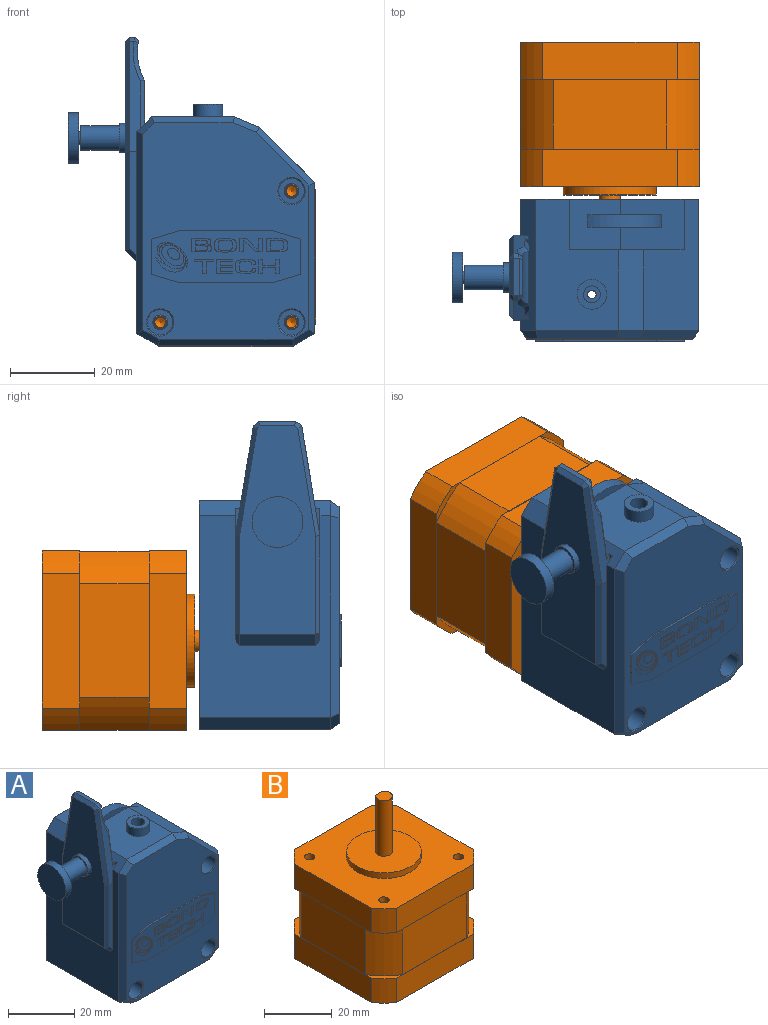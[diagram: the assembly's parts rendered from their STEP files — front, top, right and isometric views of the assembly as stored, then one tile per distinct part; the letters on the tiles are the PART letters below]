
ASSEMBLY  parts=2 mates=1
PART A: 276 faces, bbox 58.2x33.6x72.9 mm
  f0: cone r=3mm half-angle=45deg, axis (0,-1,0), area 6.9mm2, adj f4,f23
  f1: cone r=3mm half-angle=45deg, axis (0,-1,0), area 6.9mm2, adj f3,f23
  f2: cone r=3mm half-angle=45deg, axis (0,-1,0), area 6.9mm2, adj f5,f23
  f3: cylinder r=3mm len=6mm, axis (0,-1,0), area 80.1mm2, adj f1,f92
  f4: cylinder r=3mm len=6mm, axis (0,-1,0), area 80.1mm2, adj f0,f91
  f5: cylinder r=3mm len=6mm, axis (0,-1,0), area 80.1mm2, adj f2,f90
  f6: cylinder r=11mm len=22mm, axis (0,1,0), area 138.2mm2, adj f29,f89
  f7: cylinder r=1.75mm len=10.5mm, axis (1,0,0), area 115.5mm2, adj f85,f88
  f8: cylinder r=1.5mm len=11mm, axis (1,0,0), area 103.7mm2, adj f87,f88
  f9: cylinder r=6mm len=12mm, axis (1,0,0), area 94.2mm2, adj f86,f87
  f10: cylinder r=2.88mm len=9mm, axis (1,0,0), area 162.6mm2, adj f84,f85
  f11: cylinder r=3.5mm len=7mm, axis (1,0,0), area 33mm2, adj f56,f84
  f12: cylinder r=2mm len=4mm, axis (0,0,-1), area 37.7mm2, adj f22,f52
  f13: cylinder r=3.5mm len=7mm, axis (0,0,-1), area 66mm2, adj f27,f52
  f14: cylinder r=1mm len=51mm, axis (0,0,-1), area 320.4mm2, adj f22,f51
  f15: cylinder r=8mm len=16mm, axis (0,0,-1), area 150.8mm2, adj f25,f51
  f16: cylinder r=1.75mm len=28.5mm, axis (0,1,0), area 313.4mm2, adj f29,f90
  f17: cylinder r=1.75mm len=28.5mm, axis (0,1,0), area 313.4mm2, adj f29,f91
  f18: cylinder r=1.75mm len=28.5mm, axis (0,1,0), area 313.4mm2, adj f29,f92
  f19: plane 35.32x12.32mm, normal (0,-1,0), area 302.9mm2, adj f43,f44,f45,f46,f47,f48,f49,f50
  f20: plane 15x12mm, normal (0,0,1), area 150.6mm2, adj f21,f28,f29,f93,f94,f95,f96
  f21: plane 12x12mm, normal (0.71,0,0.71), area 171.1mm2, adj f20,f27,f29,f93,f94,f95,f96
  f22: plane 4x4mm, normal (0,0,1), area 9.4mm2, adj f12,f14
  f23: plane 51.2x39.2mm, normal (0,-1,0), area 1375.8mm2, adj f0,f1,f2,f34,f35,f36,f37,f38
  f24: plane 35.61x31mm, normal (1,0,0), area 1104mm2, adj f28,f29,f33,f40
  f25: plane 32x31mm, normal (0,0,-1), area 790.9mm2, adj f15,f29,f32,f33,f41
  f26: plane 47.61x31mm, normal (-1,0,0), area 863.4mm2, adj f29,f30,f32,f37,f53,f54,f55,f61
  f27: plane 31x19.5mm, normal (0,0,1), area 428mm2, adj f13,f21,f29,f30,f31,f34,f93
  f28: plane 31x13.03mm, normal (0.71,0,0.71), area 409.4mm2, adj f20,f24,f29,f31,f38,f93
  f29: plane 54x42mm, normal (0,1,0), area 1538.3mm2, adj f6,f16,f17,f18,f20,f21,f24,f25
  f30: plane 31x3.5mm, normal (-0.71,0,0.71), area 104mm2, adj f26,f27,f29,f35,f59,f60,f61,f62
  f31: plane 19x5.98mm, normal (0.38,0,0.92), area 122.9mm2, adj f27,f28,f36,f93
  f32: plane 31x5mm, normal (-0.5,0,-0.87), area 179mm2, adj f25,f26,f29,f39
  f33: plane 31x5mm, normal (0.5,0,-0.87), area 179mm2, adj f24,f25,f29,f42
  f34: plane 19.5x2mm, normal (0,-0.57,0.82), area 46.6mm2, adj f23,f27,f35,f36
  f35: plane 4.08x4.08mm, normal (-0.58,-0.57,0.58), area 10.7mm2, adj f23,f30,f34,f37
  f36: plane 6.25x3.66mm, normal (0.31,-0.57,0.76), area 15.1mm2, adj f23,f31,f34,f38
  f37: plane 47.61x2mm, normal (-0.82,-0.57,0), area 114.6mm2, adj f23,f26,f35,f39
  f38: plane 13.82x13.61mm, normal (0.58,-0.57,0.58), area 43.9mm2, adj f23,f28,f36,f40
  f39: plane 5.38x3.7mm, normal (-0.41,-0.57,-0.71), area 12.7mm2, adj f23,f32,f37,f41
  f40: plane 35.61x2mm, normal (0.82,-0.57,0), area 85.3mm2, adj f23,f24,f38,f42
  f41: plane 32x2mm, normal (0,-0.57,-0.82), area 77.2mm2, adj f23,f25,f39,f42
  f42: plane 5.38x3.7mm, normal (0.41,-0.57,-0.71), area 12.7mm2, adj f23,f33,f40,f41
  f43: plane 6.66x2mm, normal (0.29,0,-0.96), area 3.5mm2, adj f19,f23,f44,f50
  f44: plane 21.99x0.5mm, normal (0,0,-1), area 11mm2, adj f19,f23,f43,f45
  f45: plane 6.66x2mm, normal (-0.29,0,-0.96), area 3.5mm2, adj f19,f23,f44,f46
  f46: plane 8.3x0.5mm, normal (-1,0,0), area 4.2mm2, adj f19,f23,f45,f47
  f47: plane 6.66x2mm, normal (-0.29,0,0.96), area 3.5mm2, adj f19,f23,f46,f48
  f48: plane 21.99x0.5mm, normal (0,0,1), area 11mm2, adj f19,f23,f47,f49
  f49: plane 6.66x2mm, normal (0.29,0,0.96), area 3.5mm2, adj f19,f23,f48,f50
  f50: plane 8.3x0.5mm, normal (1,0,0), area 4.2mm2, adj f19,f23,f43,f49
  f51: plane 16x16mm, normal (0,0,-1), area 197.9mm2, adj f14,f15
  f52: plane 7x7mm, normal (0,0,1), area 25.9mm2, adj f12,f13
  f53: plane 24.54x1.7mm, normal (0,-1,0), area 40.3mm2, adj f26,f65,f82,f83
  f54: plane 24.54x1.7mm, normal (0,1,0), area 40.3mm2, adj f26,f62,f75,f76
  f55: plane 18x2.7mm, normal (-0.71,0,-0.71), area 68.7mm2, adj f26,f56,f75,f83
  f56: plane 49.25x18mm, normal (-1,0,0), area 734.7mm2, adj f11,f55,f76,f77,f78,f79,f80,f81
  f57: plane 8.82x1.26mm, normal (0,0,1), area 11.1mm2, adj f66,f67,f70,f71,f72,f79
  f58: cylinder r=13.85mm len=12.41mm, axis (0,1,0), area 103.2mm2, adj f59,f68,f69,f70,f71,f72,f73,f74
  f59: plane 15.8x10.33mm, normal (1,0,0), area 145.5mm2, adj f30,f58,f68,f74
  f60: plane 6.55x1.09mm, normal (-1,0,0), area 3.6mm2, adj f30,f61,f62
  f61: plane 6.55x1.8mm, normal (0,-1,0), area 10.2mm2, adj f26,f30,f60,f62
  f62: plane 25.8x4.28mm, normal (0,0.99,0.16), area 59.8mm2, adj f30,f54,f60,f61,f66,f73,f74,f77
  f63: plane 6.55x1.09mm, normal (-1,0,0), area 3.6mm2, adj f30,f64,f65
  f64: plane 6.55x1.8mm, normal (0,1,0), area 10.2mm2, adj f26,f30,f63,f65
  f65: plane 26.01x4.32mm, normal (0,-0.99,0.16), area 60mm2, adj f30,f53,f63,f64,f67,f68,f69,f81
  f66: plane 1.23x1.2mm, normal (0,0.71,0.71), area 1.9mm2, adj f57,f62,f72,f73,f78
  f67: plane 1.38x1.24mm, normal (0,-0.58,0.81), area 1.9mm2, adj f57,f65,f69,f70,f80
  f68: plane 11.38x2.9mm, normal (0.71,-0.7,0.12), area 15.5mm2, adj f30,f58,f59,f65,f69
  f69: bspline ~9.52x2.69mm, area 13.8mm2, adj f58,f65,f67,f68,f70
  f70: bspline ~1.95x1.79mm, area 1.4mm2, adj f57,f58,f67,f69,f71
  f71: plane 8.79x0.84mm, normal (0.71,0,0.71), area 9.7mm2, adj f57,f58,f70,f72
  f72: bspline ~1.96x1.86mm, area 1.4mm2, adj f57,f58,f66,f71,f73
  f73: bspline ~9.42x2.69mm, area 13.7mm2, adj f58,f62,f66,f72,f74
  f74: plane 11.39x2.91mm, normal (0.71,0.7,0.12), area 15.5mm2, adj f30,f58,f59,f62,f73
  f75: plane 3.11x2.7mm, normal (-0.5,0.71,-0.5), area 4.4mm2, adj f26,f54,f55,f76
  f76: plane 23.25x1mm, normal (-0.71,0.71,0), area 32.5mm2, adj f54,f56,f75,f77
  f77: plane 25.88x5.22mm, normal (-0.71,0.7,0.12), area 36.7mm2, adj f56,f62,f76,f78
  f78: plane 1.68x1.61mm, normal (-0.71,0.5,0.5), area 1.9mm2, adj f56,f66,f77,f79
  f79: plane 8.82x1mm, normal (-0.71,0,0.71), area 12mm2, adj f56,f57,f78,f80
  f80: plane 1.7x1.56mm, normal (-0.71,-0.41,0.58), area 1.9mm2, adj f56,f67,f79,f81
  f81: plane 26.09x5.24mm, normal (-0.71,-0.7,0.12), area 36.9mm2, adj f56,f65,f80,f82
  f82: plane 23.25x1mm, normal (-0.71,-0.71,0), area 32.5mm2, adj f53,f56,f81,f83
  f83: plane 3.11x2.7mm, normal (-0.5,-0.71,-0.5), area 4.4mm2, adj f26,f53,f55,f82
  f84: plane 7x7mm, normal (-1,0,0), area 12.5mm2, adj f10,f11
  f85: plane 5.75x5.75mm, normal (-1,0,0), area 16.3mm2, adj f7,f10
  f86: plane 12x12mm, normal (-1,0,0), area 113.1mm2, adj f9
  f87: plane 12x12mm, normal (1,0,0), area 106mm2, adj f8,f9
  f88: plane 3.5x3.5mm, normal (-1,0,0), area 2.6mm2, adj f7,f8
  f89: plane 22x22mm, normal (0,1,0), area 380.1mm2, adj f6
  f90: plane 6x6mm, normal (0,-1,0), area 18.7mm2, adj f5,f16
  f91: plane 6x6mm, normal (0,-1,0), area 18.7mm2, adj f4,f17
  f92: plane 6x6mm, normal (0,-1,0), area 18.7mm2, adj f3,f18
  f93: plane 27x12mm, normal (0,1,0), area 175.7mm2, adj f20,f21,f27,f28,f31
  f94: cylinder r=13mm len=17.46mm, axis (0,1,0), area 64.2mm2, adj f20,f21,f95,f96
  f95: plane 17.46x8.75mm, normal (0,-1,0), area 92.5mm2, adj f20,f21,f94
  f96: plane 17.46x8.75mm, normal (0,1,0), area 92.5mm2, adj f20,f21,f94
  f97: extruded ~1.55x0.73mm, area 0.2mm2, adj f19,f98,f105,f106
  f98: extruded ~1.11x0.12mm, area 0.1mm2, adj f19,f97,f99,f106
  f99: extruded ~0.75x0.1mm, area 0.1mm2, adj f19,f98,f100,f106
  f100: extruded ~1.46x0.61mm, area 0.2mm2, adj f19,f99,f101,f106
  f101: extruded ~2.8x1.93mm, area 0.4mm2, adj f19,f100,f102,f106
  f102: extruded ~2.12x0.3mm, area 0.2mm2, adj f19,f101,f103,f106
  f103: extruded ~0.61x0.21mm, area 0.1mm2, adj f19,f102,f104,f106
  f104: extruded ~2.24x0.4mm, area 0.2mm2, adj f19,f103,f105,f106
  f105: extruded ~1.92x1.61mm, area 0.3mm2, adj f19,f97,f104,f106
  f106: plane 5.64x4.71mm, normal (0,-1,0), area 1.5mm2, adj f97,f98,f99,f100,f101,f102,f103,f104
  f107: plane 0.9x0.1mm, normal (0,0,-1), area 0.1mm2, adj f19,f108,f114,f115
  f108: plane 2.72x0.1mm, normal (1,0,0), area 0.3mm2, adj f19,f107,f109,f115
  f109: plane 1.82x0.1mm, normal (0,0,-1), area 0.2mm2, adj f19,f108,f110,f115
  f110: plane 0.44x0.1mm, normal (1,0,0), area 0mm2, adj f19,f109,f111,f115
  f111: plane 4.51x0.1mm, normal (0,0,1), area 0.5mm2, adj f19,f110,f112,f115
  f112: plane 0.44x0.1mm, normal (-1,0,0), area 0mm2, adj f19,f111,f113,f115
  f113: plane 1.79x0.1mm, normal (0,0,-1), area 0.2mm2, adj f19,f112,f114,f115
  f114: plane 2.72x0.1mm, normal (-1,0,0), area 0.3mm2, adj f19,f107,f113,f115
  f115: plane 4.51x3.15mm, normal (0,-1,0), area 4.4mm2, adj f107,f108,f109,f110,f111,f112,f113,f114
  f116: plane 2.85x0.1mm, normal (0,0,1), area 0.3mm2, adj f19,f117,f127,f128
  f117: plane 0.94x0.1mm, normal (1,0,0), area 0.1mm2, adj f19,f116,f118,f128
  f118: plane 2.99x0.1mm, normal (0,0,-1), area 0.3mm2, adj f19,f117,f119,f128
  f119: plane 0.41x0.1mm, normal (1,0,0), area 0mm2, adj f19,f118,f120,f128
  f120: plane 3.88x0.1mm, normal (0,0,1), area 0.4mm2, adj f19,f119,f121,f128
  f121: plane 3.15x0.1mm, normal (-1,0,0), area 0.3mm2, adj f19,f120,f122,f128
  f122: plane 3.9x0.1mm, normal (0,0,-1), area 0.4mm2, adj f19,f121,f123,f128
  f123: plane 0.41x0.1mm, normal (1,0,0), area 0mm2, adj f19,f122,f124,f128
  f124: plane 3x0.1mm, normal (0,0,1), area 0.3mm2, adj f19,f123,f125,f128
  f125: plane 1.03x0.1mm, normal (1,0,0), area 0.1mm2, adj f19,f124,f126,f128
  f126: plane 2.85x0.1mm, normal (0,0,-1), area 0.3mm2, adj f19,f125,f127,f128
  f127: plane 0.37x0.1mm, normal (1,0,0), area 0mm2, adj f19,f116,f126,f128
  f128: plane 3.9x3.15mm, normal (0,-1,0), area 6.3mm2, adj f116,f117,f118,f119,f120,f121,f122,f123
  f129: extruded ~2.07x0.23mm, area 0.2mm2, adj f19,f130,f150,f151
  f130: extruded ~0.78x0.36mm, area 0.1mm2, adj f19,f129,f131,f151
  f131: plane 0.11x0.1mm, normal (1,0,0), area 0mm2, adj f19,f130,f132,f151
  f132: plane 0.9x0.1mm, normal (0,0,1), area 0.1mm2, adj f19,f131,f133,f151
  f133: cylinder r=0.76mm len=0.15mm, axis (0,1,0), area 0mm2, adj f19,f132,f134,f151
  f134: extruded ~1.53x0.55mm, area 0.2mm2, adj f19,f133,f135,f151
  f135: extruded ~1.33x0.25mm, area 0.1mm2, adj f19,f134,f136,f151
  f136: extruded ~1.24x0.16mm, area 0.1mm2, adj f19,f135,f137,f151
  f137: extruded ~0.77x0.26mm, area 0.1mm2, adj f19,f136,f138,f151
  f138: extruded ~1.48x0.13mm, area 0.1mm2, adj f19,f137,f139,f151
  f139: extruded ~1.06x0.16mm, area 0.1mm2, adj f19,f138,f140,f151
  f140: extruded ~0.46x0.13mm, area 0mm2, adj f19,f139,f141,f151
  f141: plane 0.9x0.1mm, normal (0,0,-1), area 0.1mm2, adj f19,f140,f142,f151
  f142: extruded ~0.35x0.1mm, area 0mm2, adj f19,f141,f143,f151
  f143: extruded ~0.57x0.56mm, area 0.1mm2, adj f19,f142,f144,f151
  f144: extruded ~1.4x0.12mm, area 0.1mm2, adj f19,f143,f145,f151
  f145: extruded ~1.29x0.1mm, area 0.1mm2, adj f19,f144,f146,f151
  f146: extruded ~1.31x0.48mm, area 0.1mm2, adj f19,f145,f147,f151
  f147: extruded ~0.79x0.18mm, area 0.1mm2, adj f19,f146,f148,f151
  f148: extruded ~0.86x0.1mm, area 0.1mm2, adj f19,f147,f149,f151
  f149: extruded ~0.87x0.61mm, area 0.1mm2, adj f19,f148,f150,f151
  f150: extruded ~1.77x0.18mm, area 0.2mm2, adj f19,f129,f149,f151
  f151: plane 4.84x3.21mm, normal (0,-1,0), area 6.6mm2, adj f129,f130,f131,f132,f133,f134,f135,f136
  f152: plane 0.9x0.1mm, normal (0,0,-1), area 0.1mm2, adj f19,f153,f163,f164
  f153: plane 3.15x0.1mm, normal (1,0,0), area 0.3mm2, adj f19,f152,f154,f164
  f154: plane 0.9x0.1mm, normal (0,0,1), area 0.1mm2, adj f19,f153,f155,f164
  f155: plane 1.34x0.1mm, normal (-1,0,0), area 0.1mm2, adj f19,f154,f156,f164
  f156: plane 3.07x0.1mm, normal (0,0,1), area 0.3mm2, adj f19,f155,f157,f164
  f157: plane 1.34x0.1mm, normal (1,0,0), area 0.1mm2, adj f19,f156,f158,f164
  f158: plane 0.9x0.1mm, normal (0,0,1), area 0.1mm2, adj f19,f157,f159,f164
  f159: plane 3.15x0.1mm, normal (-1,0,0), area 0.3mm2, adj f19,f158,f160,f164
  f160: plane 0.9x0.1mm, normal (0,0,-1), area 0.1mm2, adj f19,f159,f161,f164
  f161: plane 1.4x0.1mm, normal (1,0,0), area 0.1mm2, adj f19,f160,f162,f164
  f162: plane 3.07x0.1mm, normal (0,0,-1), area 0.3mm2, adj f19,f161,f163,f164
  f163: plane 1.4x0.1mm, normal (-1,0,0), area 0.1mm2, adj f19,f152,f162,f164
  f164: plane 4.86x3.15mm, normal (0,-1,0), area 6.9mm2, adj f152,f153,f154,f155,f156,f157,f158,f159
  f165: plane 4.98x3.15mm, normal (0,-1,0), area 7.9mm2, adj f166,f167,f168,f169,f170,f171,f172,f173
  f166: extruded ~1.1x0.54mm, area 0.1mm2, adj f19,f165,f167,f173
  f167: extruded ~1.65x0.27mm, area 0.2mm2, adj f19,f165,f166,f168
  f168: plane 2.79x0.1mm, normal (0,0,1), area 0.3mm2, adj f19,f165,f167,f169
  f169: plane 3.15x0.1mm, normal (-1,0,0), area 0.3mm2, adj f19,f165,f168,f170
  f170: plane 2.9x0.1mm, normal (0,0,-1), area 0.3mm2, adj f19,f165,f169,f171
  f171: extruded ~0.81x0.1mm, area 0.1mm2, adj f19,f165,f170,f172
  f172: extruded ~0.98x0.4mm, area 0.1mm2, adj f19,f165,f171,f173
  f173: extruded ~1.33x0.29mm, area 0.1mm2, adj f19,f165,f166,f172
  f174: extruded ~1.15x0.19mm, area 0.1mm2, adj f165,f175,f180,f181
  f175: extruded ~0.94x0.29mm, area 0.1mm2, adj f165,f174,f176,f181
  f176: extruded ~0.99x0.27mm, area 0.1mm2, adj f165,f175,f177,f181
  f177: extruded ~1.07x0.19mm, area 0.1mm2, adj f165,f176,f178,f181
  f178: plane 1.84x0.1mm, normal (0,0,-1), area 0.2mm2, adj f165,f177,f179,f181
  f179: plane 2.32x0.1mm, normal (1,0,0), area 0.2mm2, adj f165,f178,f180,f181
  f180: plane 1.74x0.1mm, normal (0,0,1), area 0.2mm2, adj f165,f174,f179,f181
  f181: plane 3.18x2.32mm, normal (0,-1,0), area 7mm2, adj f174,f175,f176,f177,f178,f179,f180
  f182: extruded ~0.81x0.77mm, area 0.1mm2, adj f19,f183,f197,f198
  f183: plane 2.06x1.93mm, normal (-0.68,0,-0.73), area 0.3mm2, adj f19,f182,f184,f198
  f184: plane 1.5x0.1mm, normal (0,0,-1), area 0.2mm2, adj f19,f183,f185,f198
  f185: plane 3.15x0.1mm, normal (1,0,0), area 0.3mm2, adj f19,f184,f186,f198
  f186: plane 0.9x0.1mm, normal (0,0,1), area 0.1mm2, adj f19,f185,f187,f198
  f187: plane 2.1x0.1mm, normal (-1,0,0), area 0.2mm2, adj f19,f186,f188,f198
  f188: extruded ~0.65x0.1mm, area 0.1mm2, adj f19,f187,f189,f198
  f189: plane 0.1x0.03mm, normal (0,0,1), area 0mm2, adj f19,f188,f190,f198
  f190: extruded ~1.01x1.01mm, area 0.1mm2, adj f19,f189,f191,f198
  f191: plane 1.82x1.74mm, normal (0.69,0,0.72), area 0.3mm2, adj f19,f190,f192,f198
  f192: plane 1.49x0.1mm, normal (0,0,1), area 0.1mm2, adj f19,f191,f193,f198
  f193: plane 3.15x0.1mm, normal (-1,0,0), area 0.3mm2, adj f19,f192,f194,f198
  f194: plane 0.89x0.1mm, normal (0,0,-1), area 0.1mm2, adj f19,f193,f195,f198
  f195: plane 2.08x0.1mm, normal (1,0,0), area 0.2mm2, adj f19,f194,f196,f198
  f196: extruded ~0.66x0.1mm, area 0.1mm2, adj f19,f195,f197,f198
  f197: plane 0.1x0.04mm, normal (0,0,-1), area 0mm2, adj f19,f182,f196,f198
  f198: plane 5.23x3.15mm, normal (0,-1,0), area 8.8mm2, adj f182,f183,f184,f185,f186,f187,f188,f189
  f199: plane 5.11x3.21mm, normal (0,-1,0), area 7.5mm2, adj f200,f201,f202,f203,f204,f205,f206,f207
  f200: extruded ~3.87x0.37mm, area 0.4mm2, adj f19,f199,f201,f206
  f201: extruded ~2.17x0.35mm, area 0.2mm2, adj f19,f199,f200,f202
  f202: extruded ~0.8x0.55mm, area 0.1mm2, adj f19,f199,f201,f203
  f203: extruded ~3.27x0.11mm, area 0.3mm2, adj f19,f199,f202,f204
  f204: extruded ~0.83x0.56mm, area 0.1mm2, adj f19,f199,f203,f205
  f205: extruded ~1.73x0.11mm, area 0.2mm2, adj f19,f199,f204,f206
  f206: extruded ~0.83x0.7mm, area 0.1mm2, adj f19,f199,f200,f205
  f207: extruded ~0.66x0.42mm, area 0.1mm2, adj f199,f208,f215,f216
  f208: extruded ~1.32x0.1mm, area 0.1mm2, adj f199,f207,f209,f216
  f209: extruded ~1.47x0.33mm, area 0.2mm2, adj f199,f208,f210,f216
  f210: extruded ~0.87x0.1mm, area 0.1mm2, adj f199,f209,f211,f216
  f211: extruded ~1.05x0.28mm, area 0.1mm2, adj f199,f210,f212,f216
  f212: extruded ~1.38x0.14mm, area 0.1mm2, adj f199,f211,f213,f216
  f213: extruded ~1.28x0.1mm, area 0.1mm2, adj f199,f212,f214,f216
  f214: extruded ~0.65x0.36mm, area 0.1mm2, adj f199,f213,f215,f216
  f215: plane 0.88x0.1mm, normal (-1,0,0), area 0.1mm2, adj f199,f207,f214,f216
  f216: plane 3.31x2.38mm, normal (0,-1,0), area 7.4mm2, adj f207,f208,f209,f210,f211,f212,f213,f214
  f217: plane 4.65x3.15mm, normal (0,-1,0), area 8.6mm2, adj f218,f219,f220,f221,f222,f223,f224,f225
  f218: extruded ~0.72x0.52mm, area 0.1mm2, adj f19,f217,f219,f227
  f219: extruded ~1.23x0.11mm, area 0.1mm2, adj f19,f217,f218,f220
  f220: plane 2.74x0.1mm, normal (0,0,1), area 0.3mm2, adj f19,f217,f219,f221
  f221: plane 3.15x0.1mm, normal (-1,0,0), area 0.3mm2, adj f19,f217,f220,f222
  f222: plane 2.95x0.1mm, normal (0,0,-1), area 0.3mm2, adj f19,f217,f221,f223
  f223: extruded ~1.11x0.11mm, area 0.1mm2, adj f19,f217,f222,f224
  f224: extruded ~0.77x0.59mm, area 0.1mm2, adj f19,f217,f223,f225
  f225: extruded ~0.97x0.75mm, area 0.1mm2, adj f19,f217,f224,f226
  f226: plane 0.1x0.01mm, normal (1,0,0), area 0mm2, adj f19,f217,f225,f227
  f227: extruded ~0.81x0.68mm, area 0.1mm2, adj f19,f217,f218,f226
  f228: extruded ~0.88x0.1mm, area 0.1mm2, adj f217,f229,f234,f243
  f229: extruded ~0.43x0.28mm, area 0.1mm2, adj f217,f228,f230,f243
  f230: extruded ~0.42x0.33mm, area 0.1mm2, adj f217,f229,f231,f243
  f231: extruded ~0.62x0.1mm, area 0.1mm2, adj f217,f230,f232,f243
  f232: plane 1.75x0.1mm, normal (0,0,-1), area 0.2mm2, adj f217,f231,f233,f243
  f233: plane 0.95x0.1mm, normal (1,0,0), area 0.1mm2, adj f217,f232,f234,f243
  f234: plane 1.54x0.1mm, normal (0,0,1), area 0.2mm2, adj f217,f228,f233,f243
  f235: extruded ~1.25x0.1mm, area 0.1mm2, adj f217,f236,f241,f242
  f236: extruded ~0.42x0.3mm, area 0.1mm2, adj f217,f235,f237,f242
  f237: extruded ~0.48x0.36mm, area 0.1mm2, adj f217,f236,f238,f242
  f238: extruded ~0.94x0.1mm, area 0.1mm2, adj f217,f237,f239,f242
  f239: plane 1.55x0.1mm, normal (0,0,-1), area 0.2mm2, adj f217,f238,f240,f242
  f240: plane 1.01x0.1mm, normal (1,0,0), area 0.1mm2, adj f217,f239,f241,f242
  f241: plane 1.31x0.1mm, normal (0,0,1), area 0.1mm2, adj f217,f235,f240,f242
  f242: plane 2.85x1.01mm, normal (0,-1,0), area 2.8mm2, adj f235,f236,f237,f238,f239,f240,f241
  f243: plane 2.7x0.95mm, normal (0,-1,0), area 2.5mm2, adj f228,f229,f230,f231,f232,f233,f234
  f244: extruded ~0.71x0.2mm, area 0.1mm2, adj f19,f245,f252,f253
  f245: extruded ~2.04x0.25mm, area 0.2mm2, adj f19,f244,f246,f253
  f246: extruded ~1.51x1mm, area 0.2mm2, adj f19,f245,f247,f253
  f247: extruded ~1.54x0.45mm, area 0.2mm2, adj f19,f246,f248,f253
  f248: extruded ~1.53x1.38mm, area 0.2mm2, adj f19,f247,f249,f253
  f249: extruded ~2.62x1.38mm, area 0.3mm2, adj f19,f248,f250,f253
  f250: extruded ~1.35x0.54mm, area 0.1mm2, adj f19,f249,f251,f253
  f251: extruded ~1.29x0.51mm, area 0.1mm2, adj f19,f250,f252,f253
  f252: extruded ~1.46x0.16mm, area 0.1mm2, adj f19,f244,f251,f253
  f253: plane 4.88x3.75mm, normal (0,-1,0), area 2.3mm2, adj f244,f245,f246,f247,f248,f249,f250,f251
  f254: plane 5.29x4.97mm, normal (0,-1,0), area 12.8mm2, adj f255,f256,f257,f258,f259,f260,f261,f262
  f255: extruded ~2.81x2.58mm, area 0.4mm2, adj f19,f254,f256,f261
  f256: extruded ~1.65x0.26mm, area 0.2mm2, adj f19,f254,f255,f257
  f257: extruded ~1.38x0.67mm, area 0.2mm2, adj f19,f254,f256,f258
  f258: extruded ~2.07x1.1mm, area 0.2mm2, adj f19,f254,f257,f259
  f259: extruded ~2.25x1.17mm, area 0.3mm2, adj f19,f254,f258,f260
  f260: extruded ~1.59x0.62mm, area 0.2mm2, adj f19,f254,f259,f261
  f261: extruded ~1.64x0.27mm, area 0.2mm2, adj f19,f254,f255,f260
  f262: extruded ~1.24x0.98mm, area 0.2mm2, adj f254,f263,f265,f266
  f263: extruded ~1.83x1.74mm, area 0.3mm2, adj f254,f262,f264,f266
  f264: extruded ~1.18x1.1mm, area 0.2mm2, adj f254,f263,f265,f266
  f265: extruded ~1.65x1.53mm, area 0.2mm2, adj f254,f262,f264,f266
  f266: plane 3.1x2.91mm, normal (0,-1,0), area 5.8mm2, adj f262,f263,f264,f265
  f267: extruded ~1.82x0.79mm, area 0.2mm2, adj f19,f268,f274,f275
  f268: extruded ~1.42x0.34mm, area 0.1mm2, adj f19,f267,f269,f275
  f269: extruded ~2.39x1.09mm, area 0.3mm2, adj f19,f268,f270,f275
  f270: extruded ~2.4x1.57mm, area 0.3mm2, adj f19,f269,f271,f275
  f271: extruded ~0.95x0.44mm, area 0.1mm2, adj f19,f270,f272,f275
  f272: extruded ~3.9x2.5mm, area 0.5mm2, adj f19,f271,f273,f275
  f273: extruded ~1.7x0.45mm, area 0.2mm2, adj f19,f272,f274,f275
  f274: extruded ~2.49x0.99mm, area 0.3mm2, adj f19,f267,f273,f275
  f275: plane 7.09x3.47mm, normal (0,-1,0), area 5.7mm2, adj f267,f268,f269,f270,f271,f272,f273,f274
PART B: 50 faces, bbox 42.4x42.4x56 mm
  f0: cylinder r=2.5mm len=20mm, axis (0,0,-1), area 265.9mm2, adj f1,f2,f29,f30
  f1: plane 5x4.5mm, normal (0,0,1), area 18.6mm2, adj f0,f29
  f2: plane 22x22mm, normal (0,0,1), area 360.5mm2, adj f0,f3
  f3: cylinder r=11mm len=22mm, axis (0,0,-1), area 138.2mm2, adj f2,f8
  f4: plane 31.78x8.75mm, normal (1,0,0), area 278mm2, adj f8,f9,f10,f32
  f5: plane 31.78x8.75mm, normal (0,-1,0), area 278mm2, adj f8,f9,f11,f32
  f6: plane 31.78x8.75mm, normal (-1,0,0), area 278mm2, adj f8,f11,f12,f32
  f7: plane 31.78x8.75mm, normal (0,1,0), area 278mm2, adj f8,f10,f12,f32
  f8: plane 42.42x42.42mm, normal (0,0,1), area 1339.6mm2, adj f3,f4,f5,f6,f7,f9,f10,f11
  f9: cylinder r=26.5mm len=8.75mm, axis (0,0,-1), area 66.1mm2, adj f4,f5,f8,f32
  f10: cylinder r=26.5mm len=8.75mm, axis (0,0,-1), area 66.1mm2, adj f4,f7,f8,f32
  f11: cylinder r=26.5mm len=8.75mm, axis (0,0,-1), area 66.1mm2, adj f5,f6,f8,f32
  f12: cylinder r=26.5mm len=8.75mm, axis (0,0,-1), area 66.1mm2, adj f6,f7,f8,f32
  f13: cone r=1.25mm half-angle=59deg, axis (0,0,1), area 5.7mm2, adj f14
  f14: cylinder r=1.25mm len=2.5mm, axis (0,0,1), area 11.8mm2, adj f13,f15
  f15: plane 3x3mm, normal (0,0,1), area 2.2mm2, adj f14,f16
  f16: cylinder r=1.5mm len=6mm, axis (0,0,1), area 56.5mm2, adj f8,f15
  f17: cone r=1.25mm half-angle=59deg, axis (0,0,1), area 5.7mm2, adj f18
  f18: cylinder r=1.25mm len=2.5mm, axis (0,0,1), area 11.8mm2, adj f17,f19
  f19: plane 3x3mm, normal (0,0,1), area 2.2mm2, adj f18,f20
  f20: cylinder r=1.5mm len=6mm, axis (0,0,1), area 56.5mm2, adj f8,f19
  f21: cone r=1.25mm half-angle=59deg, axis (0,0,1), area 5.7mm2, adj f22
  f22: cylinder r=1.25mm len=2.5mm, axis (0,0,1), area 11.8mm2, adj f21,f23
  f23: plane 3x3mm, normal (0,0,1), area 2.2mm2, adj f22,f24
  f24: cylinder r=1.5mm len=6mm, axis (0,0,1), area 56.5mm2, adj f8,f23
  f25: cone r=1.25mm half-angle=59deg, axis (0,0,1), area 5.7mm2, adj f26
  f26: cylinder r=1.25mm len=2.5mm, axis (0,0,1), area 11.8mm2, adj f25,f27
  f27: plane 3x3mm, normal (0,0,1), area 2.2mm2, adj f26,f28
  f28: cylinder r=1.5mm len=6mm, axis (0,0,1), area 56.5mm2, adj f8,f27
  f29: plane 15x3mm, normal (0,1,0), area 45mm2, adj f0,f1,f30
  f30: plane 3x0.5mm, normal (0,0,1), area 1mm2, adj f0,f29
  f31: plane 42.42x42.42mm, normal (0,0,1), area 67.2mm2, adj f33,f34,f35,f36,f37,f38,f39,f40
  f32: plane 42.42x42.42mm, normal (0,0,-1), area 67.2mm2, adj f4,f5,f6,f7,f9,f10,f11,f12
  f33: cylinder r=25mm len=16.5mm, axis (0,0,1), area 181.5mm2, adj f31,f32,f34,f40
  f34: plane 26.79x16.5mm, normal (0,1,0), area 442mm2, adj f31,f32,f33,f35
  f35: cylinder r=25mm len=16.5mm, axis (0,0,1), area 181.5mm2, adj f31,f32,f34,f36
  f36: plane 26.79x16.5mm, normal (1,0,0), area 442mm2, adj f31,f32,f35,f37
  f37: cylinder r=25mm len=16.5mm, axis (0,0,1), area 181.5mm2, adj f31,f32,f36,f38
  f38: plane 26.79x16.5mm, normal (0,-1,0), area 442mm2, adj f31,f32,f37,f39
  f39: cylinder r=25mm len=16.5mm, axis (0,0,1), area 181.5mm2, adj f31,f32,f38,f40
  f40: plane 26.79x16.5mm, normal (-1,0,0), area 442mm2, adj f31,f32,f33,f39
  f41: plane 42.42x42.42mm, normal (0,0,-1), area 1748.1mm2, adj f42,f43,f44,f45,f46,f47,f48,f49
  f42: cylinder r=26.5mm len=8.75mm, axis (0,0,-1), area 66.1mm2, adj f31,f41,f48,f49
  f43: cylinder r=26.5mm len=8.75mm, axis (0,0,-1), area 66.1mm2, adj f31,f41,f47,f48
  f44: cylinder r=26.5mm len=8.75mm, axis (0,0,-1), area 66.1mm2, adj f31,f41,f46,f47
  f45: cylinder r=26.5mm len=8.75mm, axis (0,0,-1), area 66.1mm2, adj f31,f41,f46,f49
  f46: plane 31.78x8.75mm, normal (0,1,0), area 278mm2, adj f31,f41,f44,f45
  f47: plane 31.78x8.75mm, normal (-1,0,0), area 278mm2, adj f31,f41,f43,f44
  f48: plane 31.78x8.75mm, normal (0,-1,0), area 278mm2, adj f31,f41,f42,f43
  f49: plane 31.78x8.75mm, normal (1,0,0), area 278mm2, adj f31,f41,f42,f45
PLACE A t=(23.26,37.32,13.97)mm fixed
PLACE B rot(axis=(1,0,0),90deg) t=(-19.74,40.32,13.97)mm
MATE fastened A.f2 <-> B.f21  axis (0,1,0) through (-35.24,37.32,-1.53)mm
